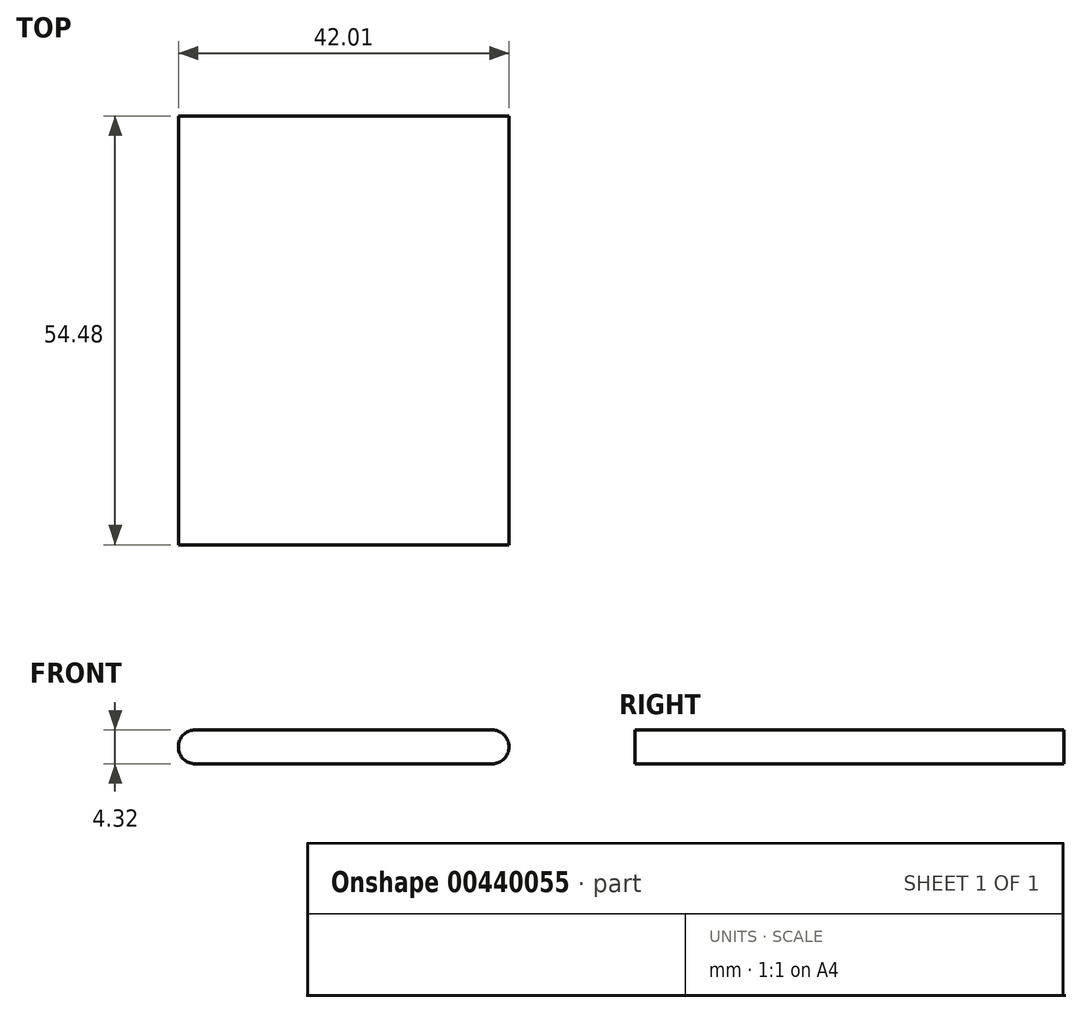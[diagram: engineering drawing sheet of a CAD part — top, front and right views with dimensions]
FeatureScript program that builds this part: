
annotation { "Feature Type Name" : "Feature", "Feature Type Description" : "" }
export const myFeature = defineFeature(function(context is Context, id is Id, definition is map)
    precondition{}
    {
        {
            var Q0;
            Q0=qCreatedBy(makeId("Top.planeOp"),FACE);
            var sketch = newSketch(context, id + "F0", { "sketchPlane" : qUnion([Q0])});
            skLineSegment(sketch, "E0.bottom", {"start": v(-26.67, 12.36) * mm, "end": v(15.34, 12.36) * mm});
            skLineSegment(sketch, "E0.top", {"start": v(-26.67, -42.12) * mm, "end": v(15.34, -42.12) * mm});
            skLineSegment(sketch, "E0.left", {"start": v(-26.67, 12.36) * mm, "end": v(-26.67, -42.12) * mm});
            skLineSegment(sketch, "E0.right", {"start": v(15.34, 12.36) * mm, "end": v(15.34, -42.12) * mm});
            skSolve(sketch);
        }
        {
            var Q0;
            Q0=makeQuery(id+"F0.imprint","IMPRINT",FACE,{"disambiguationData":[TD([[makeQuery(id+"F0.imprint","IMPRINT",EDGE,{"derivedFrom":sQuery(id+"F0.wireOp",EDGE,"E0.bottom")}),-1.0]])]});
            extrude(context, id + "F1", {"entities" : qUnion([Q0]), "depth" : 4.32 * mm});
        }
        {
            var Q0;
            Q0=makeQuery(id+"F1.opExtrude","CAP_EDGE",EDGE,{"disambiguationData":[OSD([sQuery(id+"F0.wireOp",EDGE,"E0.left")])],"isStart":false});
            var Q1;
            Q1=makeQuery(id+"F1.opExtrude","CAP_EDGE",EDGE,{"disambiguationData":[OSD([sQuery(id+"F0.wireOp",EDGE,"E0.right")])],"isStart":false});
            var Q2;
            Q2=makeQuery(id+"F1.opExtrude","CAP_EDGE",EDGE,{"disambiguationData":[OSD([sQuery(id+"F0.wireOp",EDGE,"E0.left")])],"isStart":true});
            var Q3;
            Q3=makeQuery(id+"F1.opExtrude","CAP_EDGE",EDGE,{"disambiguationData":[OSD([sQuery(id+"F0.wireOp",EDGE,"E0.right")])],"isStart":true});
            fillet(context, id + "F2", {"entities" : qUnion([Q0, Q1, Q2, Q3]), "radius" : 2.16 * mm, "tangentPropagation" : true, "allowEdgeOverflow" : false});
        }
    });
